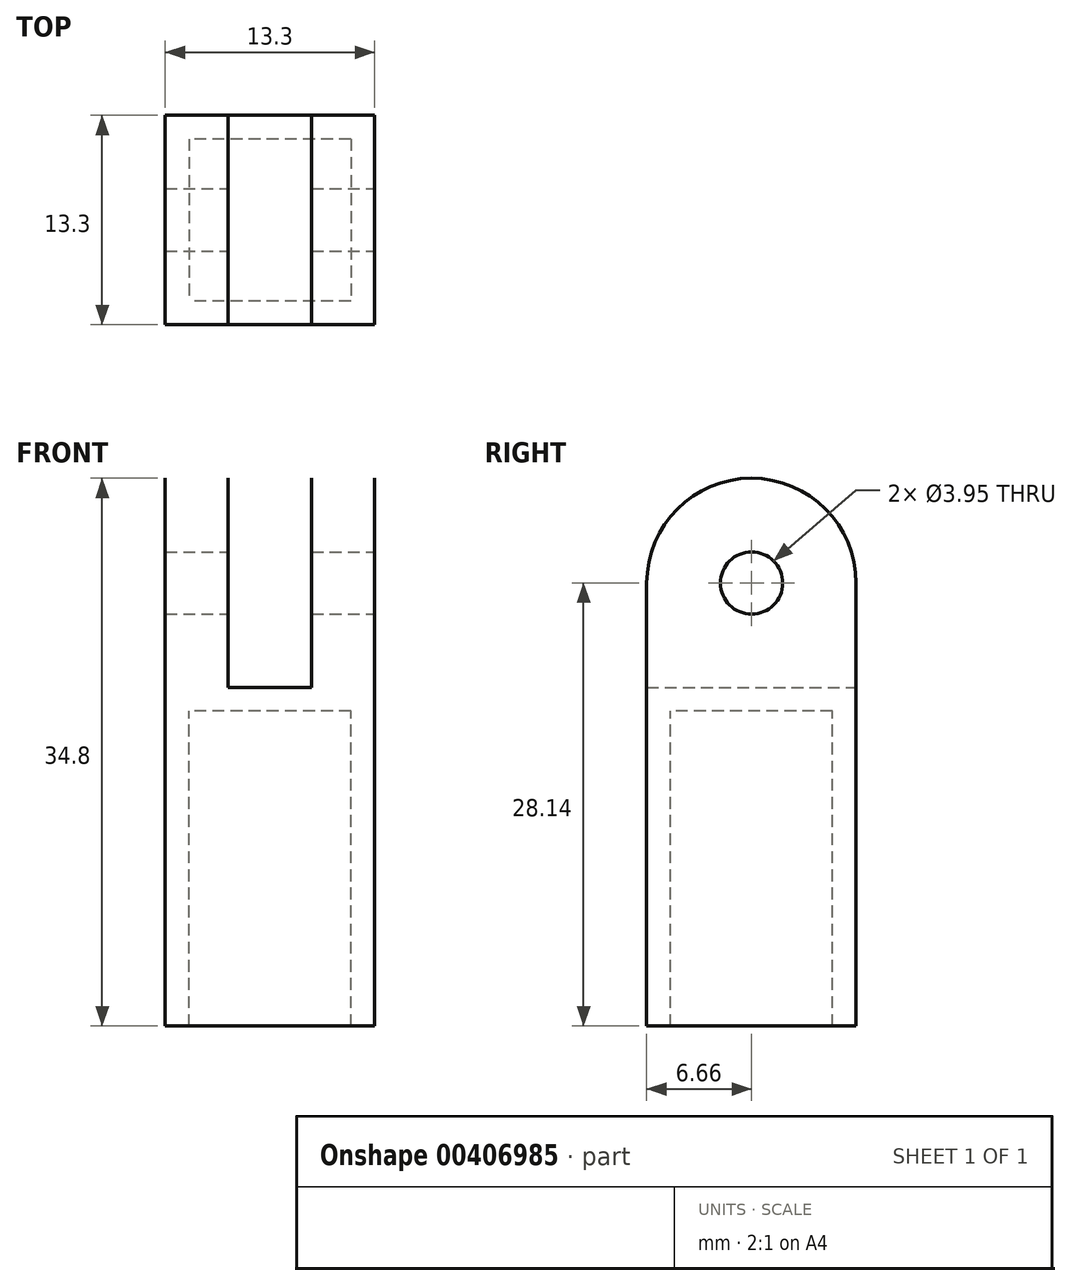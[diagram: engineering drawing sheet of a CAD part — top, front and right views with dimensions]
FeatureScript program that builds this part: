
annotation { "Feature Type Name" : "Feature", "Feature Type Description" : "" }
export const myFeature = defineFeature(function(context is Context, id is Id, definition is map)
    precondition{}
    {
        {
            var Q0;
            Q0=qCreatedBy(makeId("Top.planeOp"),FACE);
            var sketch = newSketch(context, id + "F0", { "sketchPlane" : qUnion([Q0])});
            skLineSegment(sketch, "E0.bottom", {"start": v(5.15, 5.15) * mm, "end": v(-5.15, 5.15) * mm});
            skLineSegment(sketch, "E0.top", {"start": v(5.15, -5.15) * mm, "end": v(-5.15, -5.15) * mm});
            skLineSegment(sketch, "E0.left", {"start": v(5.15, 5.15) * mm, "end": v(5.15, -5.15) * mm});
            skLineSegment(sketch, "E0.right", {"start": v(-5.15, 5.15) * mm, "end": v(-5.15, -5.15) * mm});
            skPoint(sketch, "E0.middle", {"position": v(0, 0) * mm});
            skLineSegment(sketch, "E1.bottom", {"start": v(6.65, 6.65) * mm, "end": v(-6.65, 6.65) * mm});
            skLineSegment(sketch, "E1.top", {"start": v(6.65, -6.65) * mm, "end": v(-6.65, -6.65) * mm});
            skLineSegment(sketch, "E1.left", {"start": v(6.65, 6.65) * mm, "end": v(6.65, -6.65) * mm});
            skLineSegment(sketch, "E1.right", {"start": v(-6.65, 6.65) * mm, "end": v(-6.65, -6.65) * mm});
            skSolve(sketch);
        }
        {
            var Q0;
            Q0=makeQuery(id+"F0.imprint","IMPRINT",FACE,{"disambiguationData":[TD([[makeQuery(id+"F0.imprint","IMPRINT",EDGE,{"derivedFrom":sQuery(id+"F0.wireOp",EDGE,"E0.bottom")}),-1.0]])]});
            extrude(context, id + "F1", {"entities" : qUnion([Q0]), "oppositeDirection" : true, "depth" : 20 * mm});
        }
        {
            var Q0;
            Q0=makeQuery(id+"F0.imprint","IMPRINT",FACE,{"disambiguationData":[TD([[makeQuery(id+"F0.imprint","IMPRINT",EDGE,{"derivedFrom":sQuery(id+"F0.wireOp",EDGE,"E0.bottom")}),1.0]])]});
            var Q1;
            Q1=makeQuery(id+"F0.imprint","IMPRINT",FACE,{"disambiguationData":[TD([[makeQuery(id+"F0.imprint","IMPRINT",EDGE,{"derivedFrom":sQuery(id+"F0.wireOp",EDGE,"E0.bottom")}),-1.0]])]});
            extrude(context, id + "F2", {"entities" : qUnion([Q0, Q1]), "operationType" : NewBodyOperationType.ADD, "depth" : 1.5 * mm});
        }
        {
            var Q0;
            Q0=makeQuery(id+"F2.opExtrude","CAP_FACE",FACE,{"disambiguationData":[OSD([sQuery(id+"F0.wireOp",EDGE,"E1.bottom"),sQuery(id+"F0.wireOp",EDGE,"E1.top"),sQuery(id+"F0.wireOp",EDGE,"E1.left"),sQuery(id+"F0.wireOp",EDGE,"E1.right")])],"isStart":false});
            var sketch = newSketch(context, id + "F3", { "sketchPlane" : qUnion([Q0])});
            skLineSegment(sketch, "E2.bottom", {"start": v(-6.65, -6.65) * mm, "end": v(-2.65, -6.65) * mm});
            skLineSegment(sketch, "E2.top", {"start": v(-6.65, 6.65) * mm, "end": v(-2.65, 6.65) * mm});
            skLineSegment(sketch, "E2.left", {"start": v(-6.65, -6.65) * mm, "end": v(-6.65, 6.65) * mm});
            skLineSegment(sketch, "E2.right", {"start": v(-2.65, -6.65) * mm, "end": v(-2.65, 6.65) * mm});
            skLineSegment(sketch, "E3.MirrorCS", {"start": v(2.65, -6.65) * mm, "end": v(2.65, 6.65) * mm});
            skLineSegment(sketch, "E4.MirrorCS", {"start": v(6.65, 6.65) * mm, "end": v(2.65, 6.65) * mm});
            skLineSegment(sketch, "E5.MirrorCS", {"start": v(6.65, -6.65) * mm, "end": v(6.65, 6.65) * mm});
            skLineSegment(sketch, "E6.MirrorCS", {"start": v(6.65, -6.65) * mm, "end": v(2.65, -6.65) * mm});
            skSolve(sketch);
        }
        {
            var Q0;
            Q0=makeQuery(id+"F3.imprint","IMPRINT",FACE,{"disambiguationData":[TD([[makeQuery(id+"F3.imprint","IMPRINT",EDGE,{"derivedFrom":sQuery(id+"F3.wireOp",EDGE,"E2.bottom")}),-1.0]])]});
            var Q1;
            Q1=makeQuery(id+"F3.imprint","IMPRINT",FACE,{"disambiguationData":[TD([[makeQuery(id+"F3.imprint","IMPRINT",EDGE,{"derivedFrom":sQuery(id+"F3.wireOp",EDGE,"E3.MirrorCS")}),-1.0]])]});
            extrude(context, id + "F4", {"entities" : qUnion([Q0, Q1]), "operationType" : NewBodyOperationType.ADD, "depth" : 13.3 * mm});
        }
        {
            var Q0;
            Q0=makeQuery(id+"F4.opExtrude","CAP_EDGE",EDGE,{"disambiguationData":[OSD([sQuery(id+"F3.wireOp",EDGE,"E4.MirrorCS")])],"isStart":false});
            var Q1;
            Q1=makeQuery(id+"F4.opExtrude","CAP_EDGE",EDGE,{"disambiguationData":[OSD([sQuery(id+"F3.wireOp",EDGE,"E6.MirrorCS")])],"isStart":false});
            var Q2;
            Q2=makeQuery(id+"F4.opExtrude","CAP_EDGE",EDGE,{"disambiguationData":[OSD([sQuery(id+"F3.wireOp",EDGE,"E2.top")])],"isStart":false});
            var Q3;
            Q3=makeQuery(id+"F4.opExtrude","CAP_EDGE",EDGE,{"disambiguationData":[OSD([sQuery(id+"F3.wireOp",EDGE,"E2.bottom")])],"isStart":false});
            fillet(context, id + "F5", {"entities" : qUnion([Q0, Q1, Q2, Q3]), "radius" : 6.66 * mm, "tangentPropagation" : true, "allowEdgeOverflow" : false});
        }
        {
            var Q0;
            {var subQ0=sQuery(id+"F0.wireOp",EDGE,"E1.left");Q0=makeQuery(id+"F4.boolean.opBoolean","MERGE",FACE,{"derivedFrom":[makeQuery(id+"F2.boolean.opBoolean","MERGE",FACE,{"derivedFrom":[makeQuery(id+"F1.opExtrude","SWEPT_FACE",FACE,{"disambiguationData":[OSD([subQ0])]}),makeQuery(id+"F2.opExtrude","SWEPT_FACE",FACE,{"disambiguationData":[OSD([subQ0])]})]}),makeQuery(id+"F4.opExtrude","SWEPT_FACE",FACE,{"disambiguationData":[OSD([sQuery(id+"F3.wireOp",EDGE,"E5.MirrorCS")])]})]});}
            var sketch = newSketch(context, id + "F6", { "sketchPlane" : qUnion([Q0])});
            skCircle(sketch, "E7", {"center": v(0.01, 8.14) * mm, "radius": 1.98 * mm});
            skSolve(sketch);
        }
        {
            var Q0;
            Q0=makeQuery(id+"F6.imprint","IMPRINT",FACE,{"disambiguationData":[TD([[makeQuery(id+"F6.imprint","IMPRINT",EDGE,{"derivedFrom":sQuery(id+"F6.wireOp",EDGE,"E7")}),1.0]])]});
            extrude(context, id + "F7", {"entities" : qUnion([Q0]), "operationType" : NewBodyOperationType.REMOVE, "oppositeDirection" : true, "depth" : 25 * mm, "hasSecondDirection" : true, "secondDirectionOppositeDirection" : false, "secondDirectionDepth" : 25 * mm});
        }
    });
